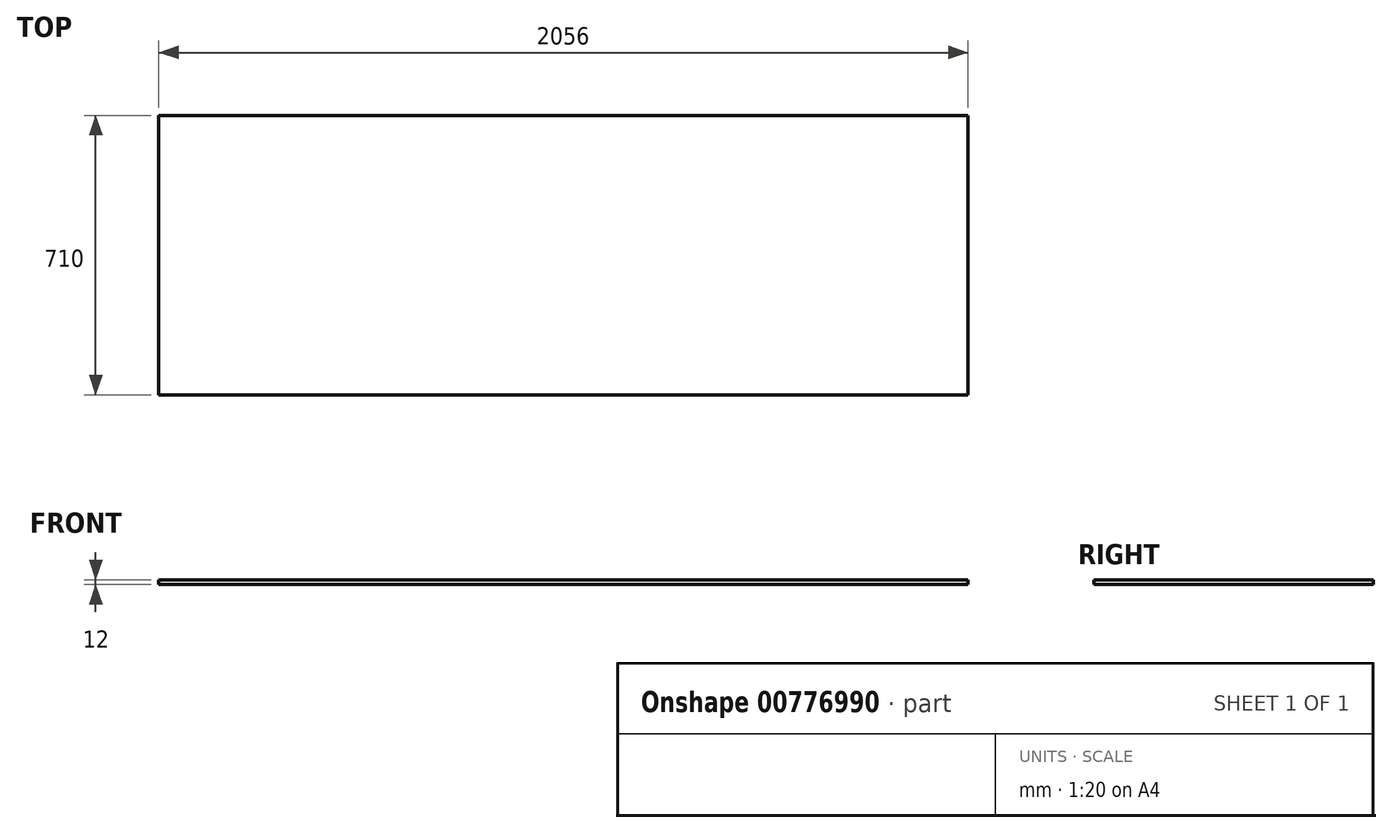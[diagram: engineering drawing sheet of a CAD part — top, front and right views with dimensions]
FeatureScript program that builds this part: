
annotation { "Feature Type Name" : "Feature", "Feature Type Description" : "" }
export const myFeature = defineFeature(function(context is Context, id is Id, definition is map)
    precondition{}
    {
        {
            var Q0;
            Q0=qCreatedBy(makeId("Top.planeOp"),FACE);
            var sketch = newSketch(context, id + "F0", { "sketchPlane" : qUnion([Q0])});
            skLineSegment(sketch, "E0.bottom", {"start": v(-1038.68, 174.9) * mm, "end": v(1017.32, 174.9) * mm});
            skLineSegment(sketch, "E0.top", {"start": v(-1038.68, -535.1) * mm, "end": v(1017.32, -535.1) * mm});
            skLineSegment(sketch, "E0.left", {"start": v(-1038.68, 174.9) * mm, "end": v(-1038.68, -535.1) * mm});
            skLineSegment(sketch, "E0.right", {"start": v(1017.32, 174.9) * mm, "end": v(1017.32, -535.1) * mm});
            skSolve(sketch);
        }
        {
            var Q0;
            Q0 = qSketchRegion(id + "F0", true);
            extrude(context, id + "F1", {"entities" : qUnion([Q0]), "depth" : 12 * mm, "offsetDistance" : 25 * mm});
        }
    });
